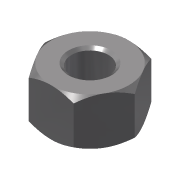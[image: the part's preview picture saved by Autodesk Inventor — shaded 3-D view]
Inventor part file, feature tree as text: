
AUTODESK INVENTOR PART (.ipt)
format: ipt  version: 2021 (Build 250183000, 183)  size: 165,376 bytes
history: native  units: in
note: dims shown in document units (in); Inventor stores cm internally (conversion verified against a paired STEP export)
features: other x14, sketch x2, extrude x1, revolve x1, mirror x1, chamfer x1
ambient origin geometry x8: Origin, YZ Plane, XZ Plane, XY Plane, X Axis, Y Axis, Z Axis, Center Point
bodies: Solid1 (feature_tree)
feature tree (20):
  other  "Table"
  other  "NUT-HEX-A194-8M-SS-0.375"
  other  "NUT-HEX-A194-8M-SS-0.500"
  other  "NUT-HEX-A194-8M-SS-0.625"
  other  "NUT-HEX-A194-8M-SS-0.750"
  other  "NUT-HEX-A194-8M-SS-0.875"
  other  "NUT-HEX-A194-8M-SS-1.000"
  other  "NUT-HEX-A194-8M-SS-1.125"
  other  "NUT-HEX-A194-8M-SS-1.250"
  other  "NUT-HEX-A194-8M-SS-1.375"
  other  "NUT-HEX-A194-8M-SS-1.500"
  other  "NUT-HEX-A194-8M-SS-1.750"
  other  "NUT-HEX-A194-8M-SS-1.875"
  other  "NUT-HEX-A194-8M-SS-2.000"
  extrude  "Extrusion1"  TaperAngle=90.0deg  [1 undecoded]
  revolve  "Revolution1"  [1 undecoded]
  mirror  "Mirror1"
  chamfer  "Chamfer2"  Distance=0.125in
  sketch  "Sketch1"  dims[d2=0.0in d8=90.0deg]
  sketch  "Sketch2"  dims[d12=0.5in d13=0.5in d21=0.125in d22=0.2405in d24=0.125in d25=0.2405in d28=0.0in]
note: 2 required parameter values undecoded (feature->parameter linkage not recoverable at this tier; creation-order binding heuristic only, values carry confidence <= 0.55)